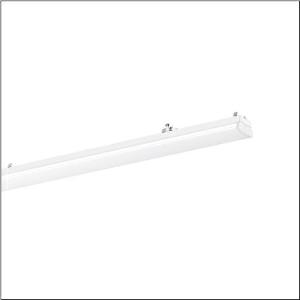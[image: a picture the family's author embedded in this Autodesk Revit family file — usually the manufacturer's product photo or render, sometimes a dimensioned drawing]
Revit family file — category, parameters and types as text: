
# Revit family: licross_r__11_recessed_opal_mo_51tl1dmn495g_9ece
name_source: partatom
category: Lighting Fixtures
units: mm (PartAtom-declared; Revit-internal decimal feet)

## family parameters
Cut with Voids When Loaded = No
Host = Face
Light Source = No
Part Type = Normal
Room Calculation Point = No
Round Connector Dimension = Use Diameter
Shared = No

## types (1)
- --- (1 x LED, 9750 lm, 55.2 W, 4000K)
    Apparent Load = 55 VA
    CIE Flux Codes = 44 73 91 87 100
    Color Rendering = 80
    Color Temperature = 4000K
    Default Elevation = 1800 mm
    Description = Licross® 11 recessed opal MO, luminaire insert, of sheet steel, coil coated, white, length: 1.500mm, width: 76mm, height: 87mm, LED rated luminous flux: 9.750lm, light colour: 840, control gear: ON/OFF Multilumen, with plug, 3-pole, with phase selection, mains connection: 220..240V, AC, 50/60Hz, rated input power: 55W, halogen-free wiring, primary optical cover: cover, of PMMA, light emission: direct with ceiling illumination distribution, primary light characteristic: symmetric, protection rating (complete): IP40, insulation class (complete): insulation class I (protective earthing), certification: CE, ENEC, VDE, UKCA, protection symbol: D if used in an environment without relevant dust loads with corresponding accessories, impact resistance: IK06, permissible ambient temperature for indoor applications: -35..+40°C, corresponds to IFS (International Featured Standards) requirements for safety and quality in the food industry, reducing of maximum allowable ambient temperature of 5°C with ceiling mounting, packaging unit: 1 piece
    Height = 83 mm
    Lamp = 1 x LED
    Lamp Light Flux = 9750 lm
    Lamp Power = 55.2 W
    Lamp count = 1
    Length = 1500 mm
    Luminous efficacy = 177 lm/W
    Manufacturer = Siteco
    ModVariant = No
    Model = 51TL1DMN495G
    Mounting Place = Ceiling
    Mounting Type = Pendant
    Number of Poles = 1
    OnlyDefault = Yes
    Power Factor = 1
    Product Name = Licross® 11 recessed opal MO
    Product group = luminaire insert
    ProductGroupID = 901
    Protection Class = Protection class I
    Protection Degree = IP 40
    RLX_Detail_Level = 1
    RLX_Emergency_Light_Flux = 0 lm
    RLX_Emergency_Type = 0
    RLX_Emergency_Type_DB = No
    RlxData = <blob elided: 24661 chars, md5=e5bc7541>
    Socket = socket
    Standby Power = 0 W
    System Light Flux = 9750 lm
    System Power = 55 W
    Type Comments = factory setting: luminous flux: 100 % | (A | C | E) | 126 mA
    Type Image = l_1313666.jpg
    URL = http://relux.com
    VarID = @adj_044811
    Voltage = 0 V
    Weight = 0.00 kg
    Width = 76 mm

## geometry (parser evidence)
native form markers: Blend x4, Sweep x11
no freeform markers — native parametric forms only
